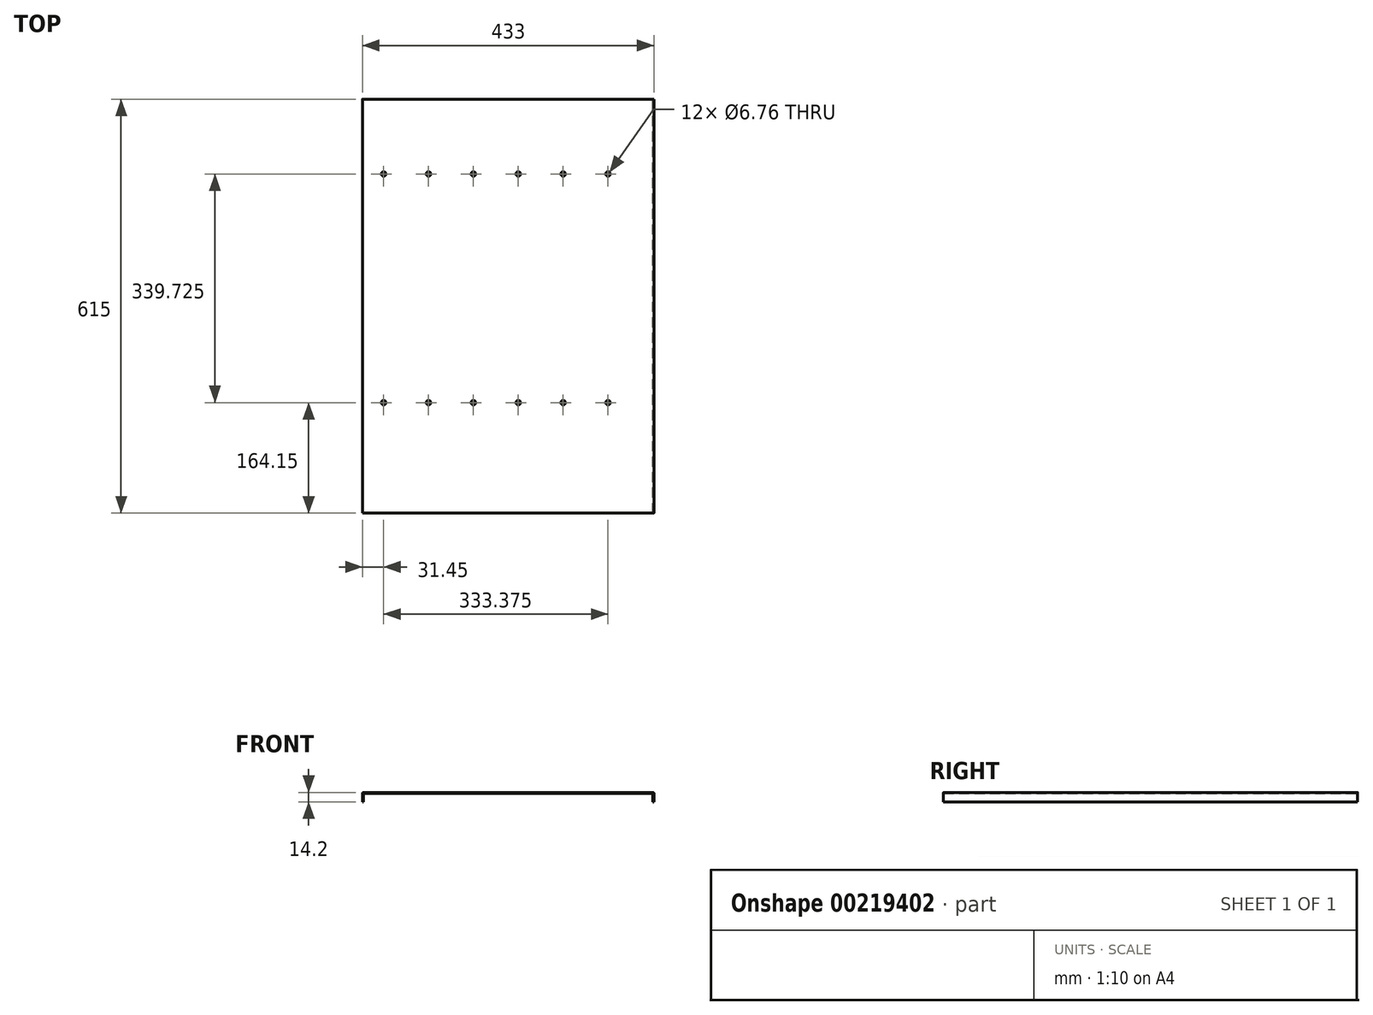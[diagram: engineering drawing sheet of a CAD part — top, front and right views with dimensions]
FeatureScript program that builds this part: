
annotation { "Feature Type Name" : "Feature", "Feature Type Description" : "" }
export const myFeature = defineFeature(function(context is Context, id is Id, definition is map)
    precondition{}
    {
        {
            var Q0;
            Q0=qCreatedBy(makeId("Top.planeOp"),FACE);
            var sketch = newSketch(context, id + "F0", { "sketchPlane" : qUnion([Q0])});
            skLineSegment(sketch, "E0.bottom", {"start": v(-216.5, -307.5) * mm, "end": v(216.5, -307.5) * mm});
            skLineSegment(sketch, "E0.top", {"start": v(-216.5, 307.5) * mm, "end": v(216.5, 307.5) * mm});
            skLineSegment(sketch, "E0.left", {"start": v(-216.5, -307.5) * mm, "end": v(-216.5, 307.5) * mm});
            skLineSegment(sketch, "E0.right", {"start": v(216.5, -307.5) * mm, "end": v(216.5, 307.5) * mm});
            skPoint(sketch, "E0.middle", {"position": v(0, 0) * mm});
            skSolve(sketch);
        }
        {
            var Q0;
            Q0=makeQuery(id+"F0.imprint","IMPRINT",FACE,{"disambiguationData":[TD([[makeQuery(id+"F0.imprint","IMPRINT",EDGE,{"derivedFrom":sQuery(id+"F0.wireOp",EDGE,"E0.bottom")}),1.0]])]});
            extrude(context, id + "F1", {"entities" : qUnion([Q0]), "depth" : 1.5 * mm});
        }
        {
            var Q0;
            Q0=makeQuery(id+"F1.opExtrude","CAP_FACE",FACE,{"disambiguationData":[OSD([sQuery(id+"F0.wireOp",EDGE,"E0.bottom"),sQuery(id+"F0.wireOp",EDGE,"E0.top"),sQuery(id+"F0.wireOp",EDGE,"E0.left"),sQuery(id+"F0.wireOp",EDGE,"E0.right")])],"isStart":true});
            var sketch = newSketch(context, id + "F2", { "sketchPlane" : qUnion([Q0])});
            skLineSegment(sketch, "E1.bottom", {"start": v(-216.5, 307.5) * mm, "end": v(-215, 307.5) * mm});
            skLineSegment(sketch, "E1.top", {"start": v(-216.5, -307.5) * mm, "end": v(-215, -307.5) * mm});
            skLineSegment(sketch, "E1.left", {"start": v(-216.5, 307.5) * mm, "end": v(-216.5, -307.5) * mm});
            skLineSegment(sketch, "E1.right", {"start": v(-215, 307.5) * mm, "end": v(-215, -307.5) * mm});
            skLineSegment(sketch, "E2.bottom", {"start": v(216.5, 307.5) * mm, "end": v(215, 307.5) * mm});
            skLineSegment(sketch, "E2.top", {"start": v(216.5, -307.5) * mm, "end": v(215, -307.5) * mm});
            skLineSegment(sketch, "E2.left", {"start": v(216.5, 307.5) * mm, "end": v(216.5, -307.5) * mm});
            skLineSegment(sketch, "E2.right", {"start": v(215, 307.5) * mm, "end": v(215, -307.5) * mm});
            skSolve(sketch);
        }
        {
            var Q0;
            Q0=makeQuery(id+"F2.imprint","IMPRINT",FACE,{"disambiguationData":[TD([[makeQuery(id+"F2.imprint","IMPRINT",EDGE,{"derivedFrom":sQuery(id+"F2.wireOp",EDGE,"E1.bottom")}),-1.0]])]});
            var Q1;
            Q1=makeQuery(id+"F2.imprint","IMPRINT",FACE,{"disambiguationData":[TD([[makeQuery(id+"F2.imprint","IMPRINT",EDGE,{"derivedFrom":sQuery(id+"F2.wireOp",EDGE,"E2.bottom")}),-1.0]])]});
            extrude(context, id + "F3", {"entities" : qUnion([Q0, Q1]), "operationType" : NewBodyOperationType.ADD, "depth" : 12.7 * mm});
        }
        {
            var Q0;
            Q0=makeQuery(id+"F1.opExtrude","CAP_EDGE",EDGE,{"disambiguationData":[OSD([sQuery(id+"F0.wireOp",EDGE,"E0.left")])],"isStart":false});
            var Q1;
            Q1=makeQuery(id+"F1.opExtrude","CAP_EDGE",EDGE,{"disambiguationData":[OSD([sQuery(id+"F0.wireOp",EDGE,"E0.right")])],"isStart":false});
            fillet(context, id + "F4", {"entities" : qUnion([Q0, Q1]), "radius" : 1.5 * mm, "tangentPropagation" : true, "allowEdgeOverflow" : false});
        }
        {
            var Q0;
            Q0=makeQuery(id+"F1.opExtrude","CAP_FACE",FACE,{"disambiguationData":[OSD([sQuery(id+"F0.wireOp",EDGE,"E0.bottom"),sQuery(id+"F0.wireOp",EDGE,"E0.top"),sQuery(id+"F0.wireOp",EDGE,"E0.left"),sQuery(id+"F0.wireOp",EDGE,"E0.right")])],"isStart":false});
            var sketch = newSketch(context, id + "F5", { "sketchPlane" : qUnion([Q0])});
            skPoint(sketch, "E3", {"position": v(148.33, 196.37) * mm});
            skPoint(sketch, "E4", {"position": v(81.65, 196.37) * mm});
            skPoint(sketch, "E5", {"position": v(14.98, 196.37) * mm});
            skPoint(sketch, "E6", {"position": v(-51.7, 196.37) * mm});
            skPoint(sketch, "E7", {"position": v(-118.37, 196.37) * mm});
            skPoint(sketch, "E8", {"position": v(148.33, -143.35) * mm});
            skPoint(sketch, "E9", {"position": v(81.65, -143.35) * mm});
            skPoint(sketch, "E10", {"position": v(14.98, -143.35) * mm});
            skPoint(sketch, "E11", {"position": v(-51.7, -143.35) * mm});
            skPoint(sketch, "E12", {"position": v(-118.37, -143.35) * mm});
            skPoint(sketch, "E13", {"position": v(-185.05, 196.37) * mm});
            skPoint(sketch, "E14", {"position": v(-185.05, -143.35) * mm});
            skSolve(sketch);
        }
        {
            var Q0;
            Q0=sQuery(id+"F5.wireOp",VERTEX,"E7");
            var Q1;
            Q1=sQuery(id+"F5.wireOp",VERTEX,"E6");
            var Q2;
            Q2=sQuery(id+"F5.wireOp",VERTEX,"E5");
            var Q3;
            Q3=sQuery(id+"F5.wireOp",VERTEX,"E4");
            var Q4;
            Q4=sQuery(id+"F5.wireOp",VERTEX,"E3");
            var Q5;
            Q5=sQuery(id+"F5.wireOp",VERTEX,"E8");
            var Q6;
            Q6=sQuery(id+"F5.wireOp",VERTEX,"E9");
            var Q7;
            Q7=sQuery(id+"F5.wireOp",VERTEX,"E10");
            var Q8;
            Q8=sQuery(id+"F5.wireOp",VERTEX,"E11");
            var Q9;
            Q9=sQuery(id+"F5.wireOp",VERTEX,"E12");
            var Q10;
            Q10=sQuery(id+"F5.wireOp",VERTEX,"E13");
            var Q11;
            Q11=sQuery(id+"F5.wireOp",VERTEX,"E14");
            var Q12;
            Q12=makeQuery(id+"F1.opExtrude","SWEPT_BODY",BODY,{"disambiguationData":[OSD([sQuery(id+"F0.wireOp",EDGE,"E0.bottom"),sQuery(id+"F0.wireOp",EDGE,"E0.top"),sQuery(id+"F0.wireOp",EDGE,"E0.left"),sQuery(id+"F0.wireOp",EDGE,"E0.right")])]});
            hole(context, id + "F6", {"style" : HoleStyle.SIMPLE, "endStyle" : HoleEndStyle.THROUGH, "standardTappedOrClearance" : lookupTablePath({ "standard" : "ANSI", "fit" : "Normal (ASME)", "size" : "1/4", "type" : "Clearance" }), "standardBlindInLast" : lookupTablePath({ "fit" : "Free", "standard" : "ANSI", "size" : "1/4", "type" : "Clearance" }), "holeDiameter" : 6.76 * mm, "locations" : qUnion([Q0, Q1, Q2, Q3, Q4, Q5, Q6, Q7, Q8, Q9, Q10, Q11]), "scope" : qUnion([Q12]), "majorDiameter" : 6.35 * mm, "tappedDepth" : 12.7 * mm, "tapClearance" : 3, "startStyle" : HoleStartStyle.SKETCH});
        }
    });
